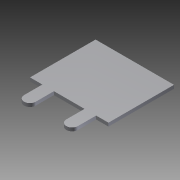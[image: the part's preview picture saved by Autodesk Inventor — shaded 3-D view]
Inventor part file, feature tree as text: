
AUTODESK INVENTOR PART (.ipt)
format: ipt  version: 2011 SP1 (Build 150282100, 282)  size: 86,528 bytes
history: native  units: in
note: dims shown in document units (in); Inventor stores cm internally (conversion verified against a paired STEP export)
features: other x7, extrude x1, sketch x1
ambient origin geometry x8: Origin, YZ Plane, XZ Plane, XY Plane, X Axis, Y Axis, Z Axis, Center Point
bodies: Solid1 (feature_tree)
feature tree (9):
  extrude  "Extrusion1"  [1 undecoded]
  other  "shtrmnl_XY"
  other  "shtrmnl_YZ"
  other  "shtrmnl_ZX"
  other  "shtrmnl_X"
  other  "shtrmnl_Y"
  other  "shtrmnl_Z"
  other  "shtrmnl_Center"
  sketch  "Sketch_1"  dims[d0=0.016in d1=0.0in]
note: 1 required parameter value undecoded (feature->parameter linkage not recoverable at this tier; creation-order binding heuristic only, values carry confidence <= 0.55)
